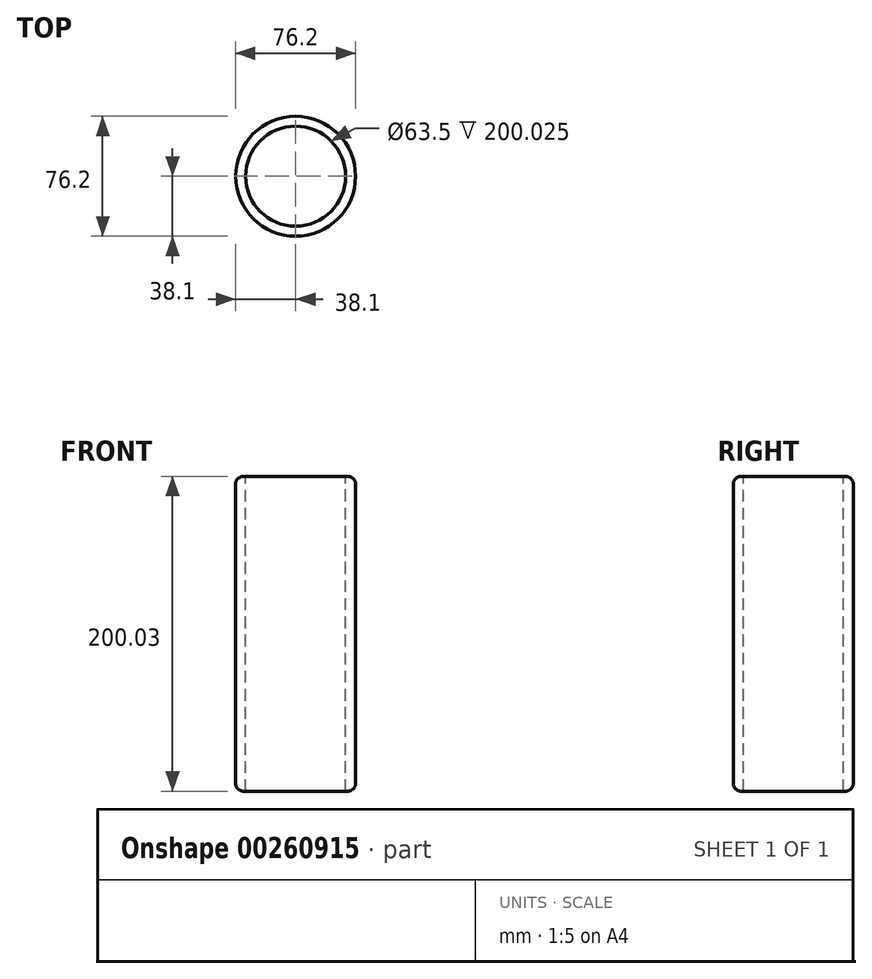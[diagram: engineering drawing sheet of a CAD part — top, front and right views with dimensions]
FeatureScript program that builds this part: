
annotation { "Feature Type Name" : "Feature", "Feature Type Description" : "" }
export const myFeature = defineFeature(function(context is Context, id is Id, definition is map)
    precondition{}
    {
        {
            var Q0;
            Q0=qCreatedBy(makeId("Top.planeOp"),FACE);
            var sketch = newSketch(context, id + "F0", { "sketchPlane" : qUnion([Q0])});
            skCircle(sketch, "E0", {"center": v(0, 0) * mm, "radius": 38.1 * mm});
            skCircle(sketch, "E1", {"center": v(0, 0) * mm, "radius": 31.75 * mm});
            skSolve(sketch);
        }
        {
            var Q0;
            Q0=makeQuery(id+"F0.imprint","IMPRINT",FACE,{"disambiguationData":[TD([[makeQuery(id+"F0.imprint","IMPRINT",EDGE,{"derivedFrom":sQuery(id+"F0.wireOp",EDGE,"E0")}),1.0]])]});
            var Q1;
            Q1=sQuery(id+"F0.wireOp",EDGE,"E0");
            extrude(context, id + "F1", {"entities" : qUnion([Q0]), "surfaceEntities" : qUnion([Q1]), "oppositeDirection" : true, "depth" : 200.02 * mm});
        }
        {
            var Q0;
            Q0=makeQuery(id+"F1.opExtrude","CAP_EDGE",EDGE,{"disambiguationData":[OSD([sQuery(id+"F0.wireOp",EDGE,"E0")])],"isStart":true});
            var Q1;
            Q1=makeQuery(id+"F1.opExtrude","CAP_EDGE",EDGE,{"disambiguationData":[OSD([sQuery(id+"F0.wireOp",EDGE,"E0")])],"isStart":false});
            fillet(context, id + "F2", {"entities" : qUnion([Q0, Q1]), "radius" : 5.08 * mm, "tangentPropagation" : true, "allowEdgeOverflow" : false});
        }
    });
